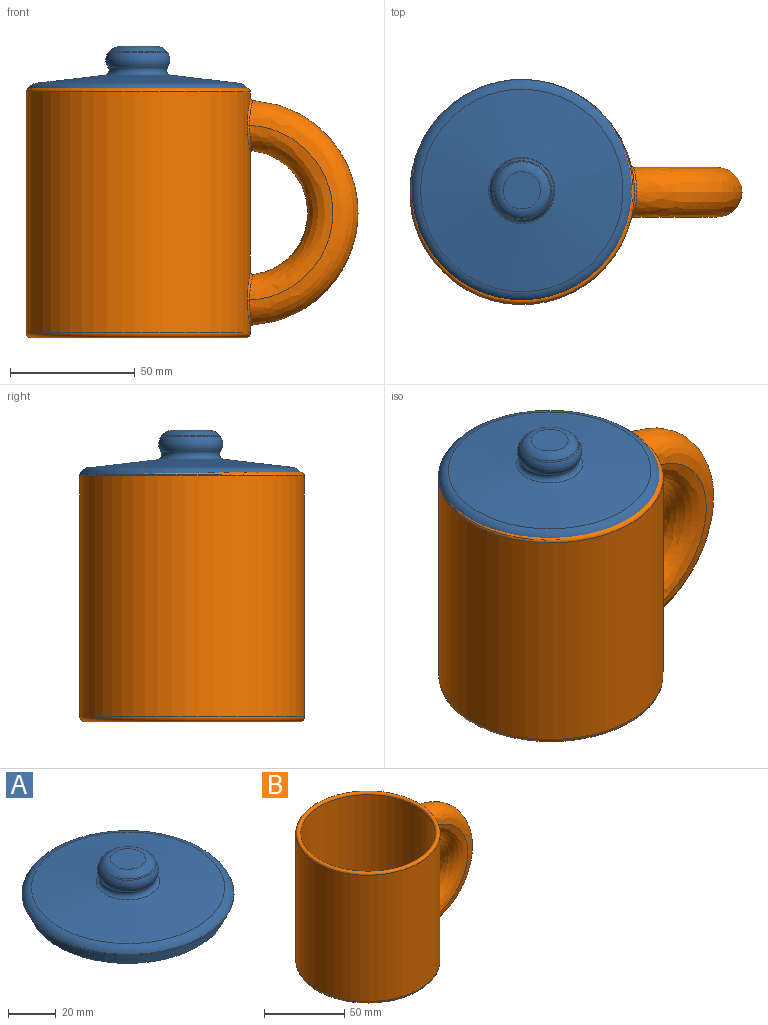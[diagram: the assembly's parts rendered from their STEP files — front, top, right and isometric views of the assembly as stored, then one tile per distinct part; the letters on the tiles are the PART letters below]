
ASSEMBLY  parts=2 mates=1
PART A: 12 faces, bbox 97.4x97.4x24.3 mm
  f0: plane 14.92x14.92mm, normal (0,0,1), area 174.9mm2, adj f9
  f1: cone r=10mm half-angle=36.2deg, axis (0,0,-1), area 46.8mm2, adj f7,f9
  f2: cone r=13.95mm half-angle=34.1deg, axis (0,0,1), area 17.6mm2, adj f7,f10
  f3: cone r=10mm half-angle=83.3deg, axis (0,0,-1), area 4648.3mm2, adj f8,f10
  f4: plane 88.06x88.06mm, normal (0,0,-1), area 679.5mm2, adj f5,f11
  f5: cylinder r=41.5mm len=83mm, axis (0,0,1), area 1564.5mm2, adj f4,f6
  f6: plane 83x83mm, normal (0,0,-1), area 5410.6mm2, adj f5
  f7: torus R=7.84mm, axis (0,0,-1), area 482.6mm2, adj f1,f2
  f8: torus R=39.99mm, axis (0,0,-1), area 1343.2mm2, adj f3,f11
  f9: torus R=7.46mm, axis (0,0,1), area 284.7mm2, adj f0,f1
  f10: torus R=13.5mm, axis (0,0,1), area 308.7mm2, adj f2,f3
  f11: torus R=44.03mm, axis (0,0,-1), area 282.4mm2, adj f4,f8
PART B: 12 faces, bbox 136.7x97.4x100 mm
  f0: cylinder r=45mm len=96.5mm, axis (0,0,-1), area 26526mm2, adj f6,f7,f8,f9,f10,f11
  f1: plane 86x86mm, normal (0,0,-1), area 5808.8mm2, adj f7
  f2: cylinder r=42mm len=95.5mm, axis (0,0,-1), area 25201.9mm2, adj f3,f6
  f3: plane 84x84mm, normal (0,0,1), area 5541.8mm2, adj f2
  f4: bspline ~90.12x43.4mm, area 3998mm2, adj f5,f9,f11
  f5: bspline ~70.04x34.3mm, area 2691.5mm2, adj f4,f8,f9,f10,f11
  f6: torus R=43.5mm, axis (0,0,1), area 1288mm2, adj f0,f2
  f7: torus R=43mm, axis (0,0,1), area 873.9mm2, adj f0,f1
  f8: bspline ~21.53x11.8mm, area 49.6mm2, adj f0,f5,f9
  f9: bspline ~21.53x11.62mm, area 46.1mm2, adj f0,f4,f5,f8
  f10: bspline ~21.53x11.8mm, area 49.6mm2, adj f0,f5,f11
  f11: bspline ~21.53x11.62mm, area 46.1mm2, adj f0,f4,f5,f10
PLACE A t=(-29.72,0.09,46.93)mm
PLACE B t=(-29.62,-0.51,36.22)mm
MATE planar A.f1 <-> B.f0  axis (0,0,-1) through (-29.72,0.09,84.72)mm
